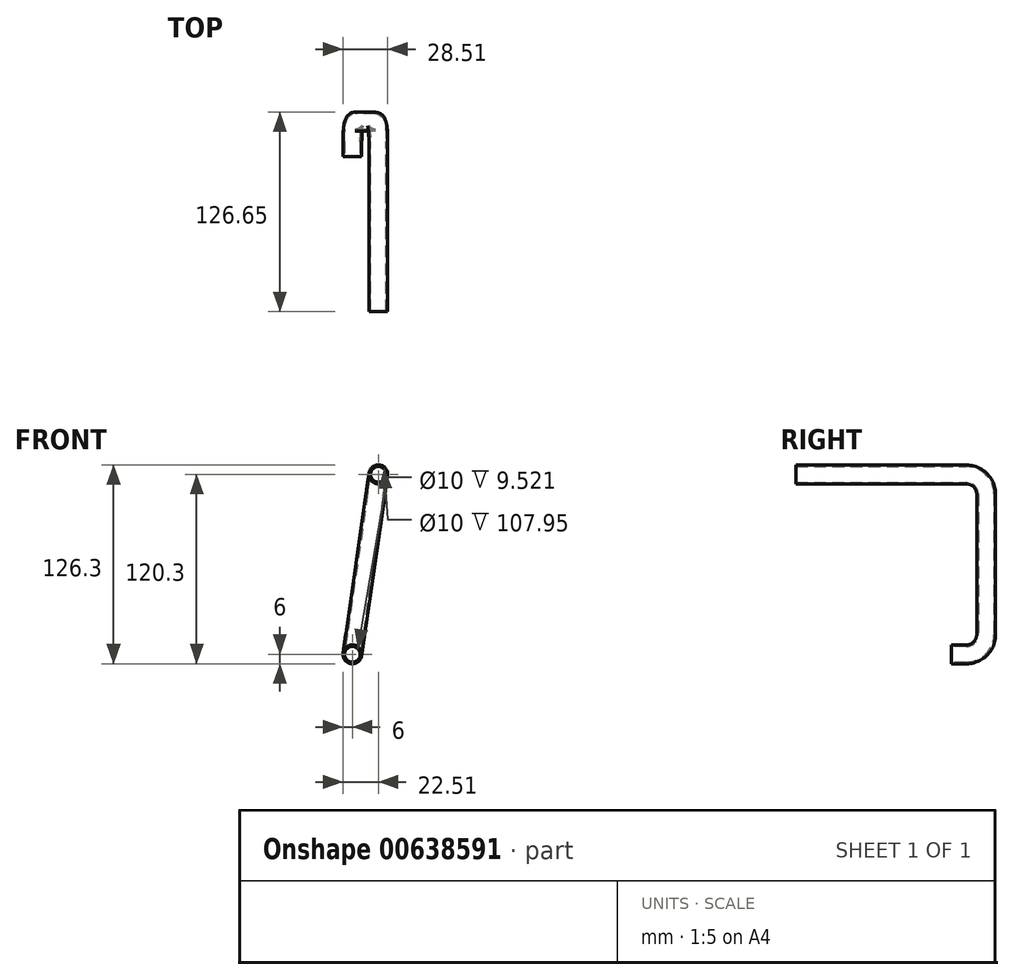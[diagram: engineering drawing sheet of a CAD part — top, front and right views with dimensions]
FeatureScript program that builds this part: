
annotation { "Feature Type Name" : "Feature", "Feature Type Description" : "" }
export const myFeature = defineFeature(function(context is Context, id is Id, definition is map)
    precondition{}
    {
        {
            var Q0;
            Q0=qCreatedBy(makeId("Front.planeOp"),FACE);
            var sketch = newSketch(context, id + "F0", { "sketchPlane" : qUnion([Q0])});
            skCircle(sketch, "E0", {"center": v(0, 0) * mm, "radius": 5 * mm});
            skCircle(sketch, "E1", {"center": v(0, 0) * mm, "radius": 6 * mm});
            skLineSegment(sketch, "E2", {"start": v(0, 0) * mm, "end": v(0, -114.3) * mm, "construction": true});
            skLineSegment(sketch, "E3", {"start": v(0, -114.3) * mm, "end": v(-16.5, -114.3) * mm, "construction": true});
            skLineSegment(sketch, "E4", {"start": v(0, 0) * mm, "end": v(-16.51, -114.3) * mm, "construction": true});
            skSolve(sketch);
        }
        {
            var Q0;
            Q0=sQuery(id+"F0.wireOp",EDGE,"E4");
            cPlane(context, id + "F1", {"entities" : qUnion([Q0]), "cplaneType" : CPlaneType.LINE_ANGLE, "offset" : 25.4 * mm, "angle" : 0 * degree, "width" : 152.4 * mm, "height" : 152.4 * mm});
        }
        {
            var Q0;
            Q0=qCreatedBy(id+"F1.planeOp",FACE);
            var sketch = newSketch(context, id + "F2", { "sketchPlane" : qUnion([Q0])});
            skLineSegment(sketch, "E5", {"start": v(0, 0) * mm, "end": v(-107.95, 0) * mm});
            skPoint(sketch, "E6.0", {"position": v(0, -115.49) * mm});
            skLineSegment(sketch, "E7", {"start": v(-120.65, -12.7) * mm, "end": v(-120.65, -102.79) * mm});
            skLineSegment(sketch, "E8", {"start": v(-107.95, -115.49) * mm, "end": v(-98.43, -115.49) * mm});
            skPoint(sketch, "E9.visualSharp", {"position": v(-120.65, 0) * mm});
            skArc(sketch, "E9.filletArc", {"start": v(-107.95, 0) * mm, "mid": v(-116.93, -3.72) * mm, "end": v(-120.65, -12.7) * mm});
            skPoint(sketch, "E10.visualSharp", {"position": v(-120.65, -115.49) * mm});
            skArc(sketch, "E10.filletArc", {"start": v(-120.65, -102.79) * mm, "mid": v(-116.93, -111.77) * mm, "end": v(-107.95, -115.49) * mm});
            skSolve(sketch);
        }
        {
            var Q0;
            Q0=makeQuery(id+"F0.imprint","IMPRINT",FACE,{"disambiguationData":[TD([[makeQuery(id+"F0.imprint","IMPRINT",EDGE,{"derivedFrom":sQuery(id+"F0.wireOp",EDGE,"E0")}),-1.0]])]});
            var Q1;
            Q1=sQuery(id+"F2.wireOp",EDGE,"E5");
            var Q2;
            Q2=sQuery(id+"F2.wireOp",EDGE,"E9.filletArc");
            var Q3;
            Q3=sQuery(id+"F2.wireOp",EDGE,"E7");
            var Q4;
            Q4=sQuery(id+"F2.wireOp",EDGE,"E10.filletArc");
            var Q5;
            Q5=sQuery(id+"F2.wireOp",EDGE,"E8");
            sweep(context, id + "F3", {"profiles" : qUnion([Q0]), "path" : qUnion([Q1, Q2, Q3, Q4, Q5])});
        }
    });
